# Revit family: Plumbing-Fixturse_Haws-Corporation_8605SS
name_source: partatom
category: Plumbing Fixtures
units: mm (PartAtom-declared; Revit-internal decimal feet)

## family parameters
Always vertical = No
Cut with Voids When Loaded = No
OmniClass Number = 23.45.05.14.17.11
Part Type = Normal
Room Calculation Point = No
Round Connector Dimension = Use Radius
Shared = No
Work Plane-Based = Yes

## types (1)
- 8605SS
    CW Connection = Yes
    CWFU = 1
    Default Elevation = 10"
    Depth = 36 1/2"
    Description = Model 8605SS combination shower and eye/face wash stainless steel.
    Flow = 20 GPM
    HW Connection = No
    HWFU = 0
    Height = 82 1/2"
    Housing Material = Haws Corporation - Metal - Satin Finish Stainless Steel
    Manufacturer = Haws Corporation
    Model = 8605SS
    Product Documentation Link = https://www.hawsco.com
    Product Page URL = https://www.hawsco.com
    Product data url = https://www.bimobject.com
    Pull Rod = Haws Corporation - Metal - High Polished Stainless Steel
    Sanitary Radius = 2"
    Supply Radius = 1/2"
    URL = https://www.hawsco.com
    Vent Connection = No
    Version = 1
    WFU = 1
    Waste Connection = Yes
    Width = 38 1/2"

## geometry (parser evidence)
native form markers: Blend x2, Sweep x5
no freeform markers — native parametric forms only
